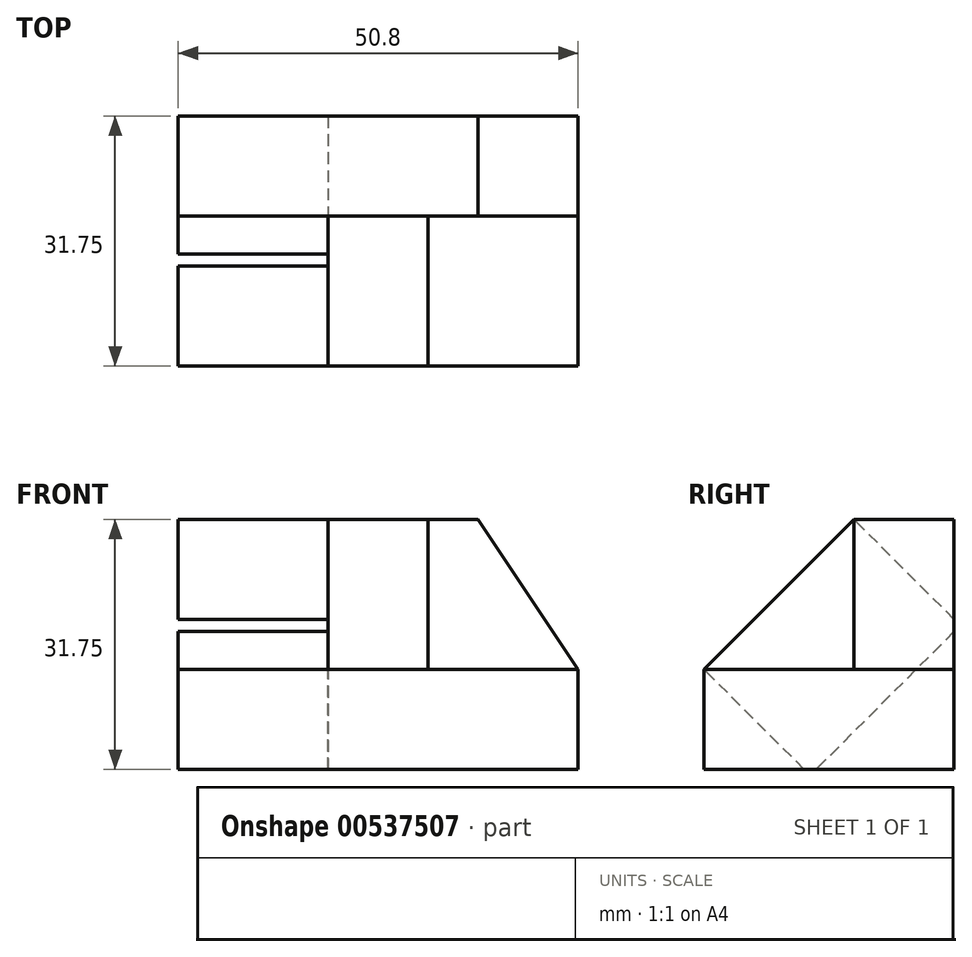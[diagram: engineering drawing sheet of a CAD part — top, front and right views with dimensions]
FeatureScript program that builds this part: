
annotation { "Feature Type Name" : "Feature", "Feature Type Description" : "" }
export const myFeature = defineFeature(function(context is Context, id is Id, definition is map)
    precondition{}
    {
        {
            var Q0;
            Q0=qCreatedBy(makeId("Right.planeOp"),FACE);
            var sketch = newSketch(context, id + "F0", { "sketchPlane" : qUnion([Q0])});
            skLineSegment(sketch, "E0", {"start": v(0, 0) * mm, "end": v(31.75, 0) * mm});
            skLineSegment(sketch, "E1", {"start": v(31.75, 0) * mm, "end": v(31.75, 31.75) * mm});
            skLineSegment(sketch, "E2", {"start": v(31.75, 31.75) * mm, "end": v(19.05, 31.75) * mm});
            skLineSegment(sketch, "E3", {"start": v(19.05, 31.75) * mm, "end": v(19.05, 12.7) * mm});
            skLineSegment(sketch, "E4", {"start": v(19.05, 12.7) * mm, "end": v(0, 12.7) * mm});
            skLineSegment(sketch, "E5", {"start": v(0, 12.7) * mm, "end": v(0, 0) * mm});
            skSolve(sketch);
        }
        {
            var Q0;
            Q0=makeQuery(id+"F0.imprint","IMPRINT",FACE,{"disambiguationData":[TD([[makeQuery(id+"F0.imprint","IMPRINT",EDGE,{"derivedFrom":sQuery(id+"F0.wireOp",EDGE,"E0")}),1.0]])]});
            extrude(context, id + "F1", {"entities" : qUnion([Q0]), "depth" : 50.8 * mm, "offsetDistance" : 25.4 * mm});
        }
        {
            var Q0;
            Q0=makeQuery(id+"F1.opExtrude","SWEPT_FACE",FACE,{"disambiguationData":[OSD([sQuery(id+"F0.wireOp",EDGE,"E3")])]});
            var sketch = newSketch(context, id + "F2", { "sketchPlane" : qUnion([Q0])});
            skLineSegment(sketch, "E6", {"start": v(50.8, 12.7) * mm, "end": v(38.1, 31.75) * mm});
            skLineSegment(sketch, "E7", {"start": v(38.1, 31.75) * mm, "end": v(0, 31.75) * mm});
            skSolve(sketch);
        }
        {
            var Q0;
            {var subQ0=sQuery(id+"F2.wireOp",EDGE,"E6");Q0=makeQuery(id+"F2.imprint","IMPRINT",FACE,{"disambiguationData":[TD([[makeQuery(id+"F2.imprint","IMPRINT",EDGE,{"derivedFrom":subQ0}),-1.0]])]});}
            extrude(context, id + "F3", {"entities" : qUnion([Q0]), "operationType" : NewBodyOperationType.REMOVE, "oppositeDirection" : true, "depth" : 25.4 * mm, "offsetDistance" : 25.4 * mm});
        }
        {
            var Q0;
            Q0=makeQuery(id+"F1.opExtrude","CAP_FACE",FACE,{"disambiguationData":[OSD([sQuery(id+"F0.wireOp",EDGE,"E0"),sQuery(id+"F0.wireOp",EDGE,"E1"),sQuery(id+"F0.wireOp",EDGE,"E2"),sQuery(id+"F0.wireOp",EDGE,"E3"),sQuery(id+"F0.wireOp",EDGE,"E4"),sQuery(id+"F0.wireOp",EDGE,"E5")])],"isStart":true});
            var sketch = newSketch(context, id + "F4", { "sketchPlane" : qUnion([Q0])});
            skLineSegment(sketch, "E8", {"start": v(-19.05, 31.75) * mm, "end": v(0, 12.7) * mm});
            skSolve(sketch);
        }
        {
            var Q0;
            Q0=makeQuery(id+"F4.imprint","IMPRINT",FACE,{"disambiguationData":[TD([[makeQuery(id+"F4.imprint","IMPRINT",EDGE,{"derivedFrom":sQuery(id+"F4.wireOp",EDGE,"E8")}),-1.0]])]});
            extrude(context, id + "F5", {"entities" : qUnion([Q0]), "oppositeDirection" : true, "depth" : 31.75 * mm, "offsetDistance" : 25.4 * mm});
        }
        {
            var Q0;
            Q0=makeQuery(id+"F5.opExtrude","SWEPT_FACE",FACE,{"disambiguationData":[OSD([sQuery(id+"F4.wireOp",EDGE,"E8")])]});
            var sketch = newSketch(context, id + "F6", { "sketchPlane" : qUnion([Q0])});
            skLineSegment(sketch, "E9", {"start": v(19.05, 35.92) * mm, "end": v(19.05, 8.98) * mm});
            skLineSegment(sketch, "E10", {"start": v(19.05, 35.92) * mm, "end": v(31.75, 35.92) * mm});
            skSolve(sketch);
        }
        {
            var Q0;
            Q0 = qSketchRegion(id + "F6", true);
            var Q1;
            {var subQ0=sQuery(id+"F6.wireOp",EDGE,"E9");Q1=makeQuery(id+"F6.imprint","IMPRINT",FACE,{"disambiguationData":[TD([[makeQuery(id+"F6.imprint","IMPRINT",EDGE,{"derivedFrom":subQ0}),1.0]])]});}
            extrude(context, id + "F7", {"entities" : qUnion([Q0, Q1]), "operationType" : NewBodyOperationType.REMOVE, "depth" : 19.05 * mm, "offsetDistance" : 25.4 * mm});
        }
        {
            var Q0;
            Q0=makeQuery(id+"F5.opExtrude","SWEPT_FACE",FACE,{"disambiguationData":[OSD([sQuery(id+"F4.wireOp",EDGE,"E8")])]});
            var sketch = newSketch(context, id + "F8", { "sketchPlane" : qUnion([Q0])});
            skLineSegment(sketch, "E11", {"start": v(19.05, 35.92) * mm, "end": v(19.05, 8.98) * mm});
            skLineSegment(sketch, "E12", {"start": v(19.05, 35.92) * mm, "end": v(31.75, 35.92) * mm});
            skSolve(sketch);
        }
        {
            var Q0;
            {var subQ0=sQuery(id+"F8.wireOp",EDGE,"E11");Q0=makeQuery(id+"F8.imprint","IMPRINT",FACE,{"disambiguationData":[TD([[makeQuery(id+"F8.imprint","IMPRINT",EDGE,{"derivedFrom":subQ0}),-1.0]])]});}
            extrude(context, id + "F9", {"entities" : qUnion([Q0]), "operationType" : NewBodyOperationType.REMOVE, "oppositeDirection" : true, "depth" : 19.05 * mm, "offsetDistance" : 25.4 * mm});
        }
    });
